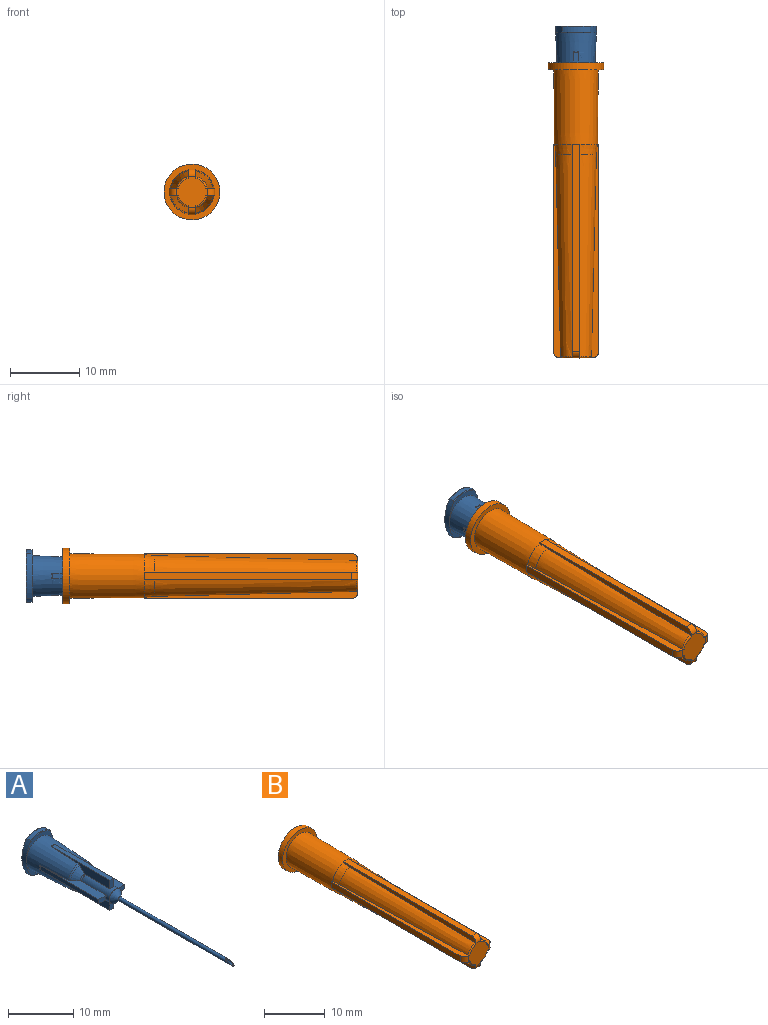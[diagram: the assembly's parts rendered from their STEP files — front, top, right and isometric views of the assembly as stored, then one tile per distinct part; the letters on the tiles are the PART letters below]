
ASSEMBLY  parts=2 mates=1
PART A: 60 faces, bbox 6x43x8.4 mm
  f0: cone r=2.51mm half-angle=44deg, axis (0,1,0), area 3.1mm2, adj f19,f22,f50,f54
  f1: cone r=2.97mm half-angle=2.9deg, axis (0,1,0), area 130.1mm2, adj f6,f7,f8,f9,f10,f11,f12,f13
  f2: cone r=2.51mm half-angle=44deg, axis (0,1,0), area 3.1mm2, adj f14,f17,f51,f55
  f3: cone r=2.51mm half-angle=44deg, axis (0,1,0), area 3.1mm2, adj f8,f12,f52,f56
  f4: cylinder r=1.28mm len=6.08mm, axis (0,1,0), area 31.5mm2, adj f8,f9,f12,f14,f17,f19,f22,f24
  f5: cone r=2.51mm half-angle=44deg, axis (0,1,0), area 3.1mm2, adj f9,f24,f49,f53
  f6: plane 0.2x0.02mm, normal (0,1,0), area 0mm2, adj f1,f7,f8
  f7: plane 12.75x0.8mm, normal (0,0,1), area 10.2mm2, adj f1,f6,f8,f9,f10,f29
  f8: plane 12.82x1.67mm, normal (-1,0,0), area 11mm2, adj f1,f3,f4,f6,f7,f29,f52,f56
  f9: plane 12.82x1.67mm, normal (1,0,0), area 11mm2, adj f1,f4,f5,f7,f10,f29,f49,f53
  f10: plane 0.2x0.02mm, normal (0,1,0), area 0mm2, adj f1,f7,f9
  f11: plane 0.2x0.02mm, normal (0,1,0), area 0mm2, adj f1,f13,f14
  f12: plane 12.82x1.67mm, normal (0,0,1), area 11mm2, adj f1,f3,f4,f13,f15,f28,f52,f56
  f13: plane 12.75x0.8mm, normal (-1,0,0), area 10.2mm2, adj f1,f11,f12,f14,f15,f28
  f14: plane 12.82x1.67mm, normal (0,0,-1), area 11mm2, adj f1,f2,f4,f11,f13,f28,f51,f55
  f15: plane 0.2x0.02mm, normal (0,1,0), area 0mm2, adj f1,f12,f13
  f16: plane 0.2x0.02mm, normal (0,1,0), area 0mm2, adj f1,f17,f18
  f17: plane 12.82x1.67mm, normal (-1,0,0), area 11mm2, adj f1,f2,f4,f16,f18,f27,f51,f55
  f18: plane 12.75x0.8mm, normal (0,0,-1), area 10.2mm2, adj f1,f16,f17,f19,f20,f27
  f19: plane 12.82x1.67mm, normal (1,0,0), area 11mm2, adj f0,f1,f4,f18,f20,f27,f50,f54
  f20: plane 0.2x0.02mm, normal (0,1,0), area 0mm2, adj f1,f18,f19
  f21: plane 0.2x0.02mm, normal (0,1,0), area 0mm2, adj f1,f23,f24
  f22: plane 12.82x1.67mm, normal (0,0,-1), area 11mm2, adj f0,f1,f4,f23,f25,f26,f50,f54
  f23: plane 12.75x0.8mm, normal (1,0,0), area 10.2mm2, adj f1,f21,f22,f24,f25,f26
  f24: plane 12.82x1.67mm, normal (0,0,1), area 11mm2, adj f1,f4,f5,f21,f23,f26,f49,f53
  f25: plane 0.2x0.02mm, normal (0,1,0), area 0mm2, adj f1,f22,f23
  f26: plane 1.6x0.8mm, normal (0,-1,0), area 1.2mm2, adj f4,f22,f23,f24
  f27: plane 1.6x0.8mm, normal (0,-1,0), area 1.2mm2, adj f4,f17,f18,f19
  f28: plane 1.6x0.8mm, normal (0,-1,0), area 1.2mm2, adj f4,f12,f13,f14
  f29: plane 1.6x0.8mm, normal (0,-1,0), area 1.2mm2, adj f4,f7,f8,f9
  f30: cone r=1.28mm half-angle=44.9deg, axis (0,1,0), area 6.8mm2, adj f4,f34
  f31: cone r=2.57mm half-angle=2.9deg, axis (0,1,0), area 106.9mm2, adj f44,f57
  f32: cylinder r=0.88mm len=4.07mm, axis (0,1,0), area 22.5mm2, adj f58,f59
  f33: cone r=1mm half-angle=44.9deg, axis (0,1,0), area 1.3mm2, adj f35,f59
  f34: cylinder r=0.33mm len=24.7mm, axis (0,1,0), area 48.7mm2, adj f30,f36
  f35: cylinder r=0.25mm len=25mm, axis (0,-1,0), area 38.2mm2, adj f33,f36
  f36: plane 1.73x0.66mm, normal (0,-0.35,0.94), area 0.4mm2, adj f34,f35
  f37: plane 7.49x5.95mm, normal (0,1,0), area 16.5mm2, adj f39,f41,f44,f45,f46
  f38: cylinder r=3.85mm len=4.04mm, axis (0,-1,0), area 3.3mm2, adj f39,f41,f46,f48
  f39: cylinder r=6.09mm len=6.55mm, axis (0,-1,0), area 6.7mm2, adj f37,f38,f40,f42,f43,f45,f46,f47
  f40: cylinder r=3.85mm len=4.04mm, axis (0,-1,0), area 3.3mm2, adj f39,f41,f45,f47
  f41: cylinder r=6.09mm len=6.55mm, axis (0,-1,0), area 6.7mm2, adj f37,f38,f40,f42,f43,f45,f46,f47
  f42: plane 5.95x3.75mm, normal (0,-1,0), area 4.8mm2, adj f1,f39,f41,f48
  f43: plane 5.95x3.75mm, normal (0,-1,0), area 4.8mm2, adj f1,f39,f41,f47
  f44: cylinder r=2.56mm len=5.13mm, axis (0,1,0), area 15.6mm2, adj f31,f37
  f45: torus R=3.75mm, axis (0,1,0), area 0.7mm2, adj f37,f39,f40,f41
  f46: torus R=3.75mm, axis (0,1,0), area 0.7mm2, adj f37,f38,f39,f41
  f47: torus R=3.75mm, axis (0,1,0), area 0.7mm2, adj f39,f40,f41,f43
  f48: torus R=3.75mm, axis (0,1,0), area 0.7mm2, adj f38,f39,f41,f42
  f49: torus R=2.03mm, axis (0,1,0), area 1.1mm2, adj f1,f5,f9,f24
  f50: torus R=2.03mm, axis (0,1,0), area 1.1mm2, adj f0,f1,f19,f22
  f51: torus R=2.03mm, axis (0,1,0), area 1.1mm2, adj f1,f2,f14,f17
  f52: torus R=2.03mm, axis (0,1,0), area 1.1mm2, adj f1,f3,f8,f12
  f53: torus R=1.58mm, axis (0,-1,0), area 0.3mm2, adj f4,f5,f9,f24
  f54: torus R=1.58mm, axis (0,-1,0), area 0.3mm2, adj f0,f4,f19,f22
  f55: torus R=1.58mm, axis (0,-1,0), area 0.3mm2, adj f2,f4,f14,f17
  f56: torus R=1.58mm, axis (0,-1,0), area 0.3mm2, adj f3,f4,f8,f12
  f57: revolved ~4.4x4.4mm, area 24.9mm2, adj f31,f58
  f58: torus R=5.88mm, axis (0,1,0), area 19.5mm2, adj f32,f57
  f59: revolved ~1.76x1.76mm, area 3.8mm2, adj f32,f33
PART B: 58 faces, bbox 33.3x63.9x33.3 mm
  f0: cylinder r=4.05mm len=8.1mm, axis (0,-1,0), area 26.7mm2, adj f1,f2
  f1: plane 8.1x8.1mm, normal (0,1,0), area 29.9mm2, adj f0,f37
  f2: plane 8.1x8.1mm, normal (0,-1,0), area 18.9mm2, adj f0,f36
  f3: cylinder r=1mm len=1.15mm, axis (0,0,-1), area 1.8mm2, adj f11,f13,f14,f15
  f4: torus R=2.1mm, axis (0,-1,0), area 0.7mm2, adj f11,f15,f16,f17
  f5: cylinder r=1mm len=1.15mm, axis (1,0,0), area 1.8mm2, adj f11,f17,f18,f19
  f6: torus R=2.1mm, axis (0,-1,0), area 0.7mm2, adj f11,f19,f20,f21
  f7: cylinder r=1mm len=1.15mm, axis (0,0,1), area 1.8mm2, adj f11,f21,f22,f24
  f8: torus R=2.1mm, axis (0,-1,0), area 0.7mm2, adj f11,f23,f24,f25
  f9: torus R=2.1mm, axis (0,-1,0), area 0.7mm2, adj f11,f12,f13,f27
  f10: cylinder r=1mm len=1.15mm, axis (-1,0,0), area 1.8mm2, adj f11,f25,f26,f27
  f11: plane 4.6x4.6mm, normal (0,-1,0), area 14.9mm2, adj f3,f4,f5,f6,f7,f8,f9,f10
  f12: cone r=3mm half-angle=1.4deg, axis (0,1,0), area 87.7mm2, adj f9,f13,f27,f28
  f13: plane 31.02x1.3mm, normal (0,0,1), area 21.3mm2, adj f3,f9,f11,f12,f14,f28,f29
  f14: plane 30x1.15mm, normal (-1,0,0), area 34.5mm2, adj f3,f13,f15,f29
  f15: plane 31.02x1.3mm, normal (0,0,-1), area 21.3mm2, adj f3,f4,f11,f14,f16,f29,f30
  f16: cone r=3mm half-angle=1.4deg, axis (0,1,0), area 87.7mm2, adj f4,f15,f17,f30
  f17: plane 31.02x1.3mm, normal (-1,0,0), area 21.3mm2, adj f4,f5,f11,f16,f18,f30,f31
  f18: plane 30x1.15mm, normal (0,0,-1), area 34.5mm2, adj f5,f17,f19,f31
  f19: plane 31.02x1.3mm, normal (1,0,0), area 21.3mm2, adj f5,f6,f11,f18,f20,f31,f32
  f20: cone r=3mm half-angle=1.4deg, axis (0,1,0), area 87.7mm2, adj f6,f19,f21,f32
  f21: plane 31.02x1.3mm, normal (0,0,-1), area 21.3mm2, adj f6,f7,f11,f20,f22,f32,f33
  f22: plane 30x1.15mm, normal (1,0,0), area 34.5mm2, adj f7,f21,f24,f33
  f23: cone r=3mm half-angle=1.4deg, axis (0,1,0), area 87.7mm2, adj f8,f24,f25,f34
  f24: plane 31.02x1.3mm, normal (0,0,1), area 21.3mm2, adj f7,f8,f11,f22,f23,f33,f34
  f25: plane 31.02x1.3mm, normal (1,0,0), area 21.3mm2, adj f8,f10,f11,f23,f26,f34,f35
  f26: plane 30x1.15mm, normal (0,0,1), area 34.5mm2, adj f10,f25,f27,f35
  f27: plane 31.02x1.3mm, normal (-1,0,0), area 21.3mm2, adj f9,f10,f11,f12,f26,f28,f35
  f28: cone r=3.12mm half-angle=4.8deg, axis (0,1,0), area 5.5mm2, adj f12,f13,f27,f36
  f29: plane 1.15x0.23mm, normal (0,1,0), area 0.2mm2, adj f13,f14,f15,f36
  f30: cone r=3.12mm half-angle=4.8deg, axis (0,1,0), area 5.5mm2, adj f15,f16,f17,f36
  f31: plane 1.15x0.23mm, normal (0,1,0), area 0.2mm2, adj f17,f18,f19,f36
  f32: cone r=3.12mm half-angle=4.8deg, axis (0,1,0), area 5.5mm2, adj f19,f20,f21,f36
  f33: plane 1.15x0.23mm, normal (0,1,0), area 0.2mm2, adj f21,f22,f24,f36
  f34: cone r=3.12mm half-angle=4.8deg, axis (0,1,0), area 5.5mm2, adj f23,f24,f25,f36
  f35: plane 1.15x0.23mm, normal (0,1,0), area 0.2mm2, adj f25,f26,f27,f36
  f36: cone r=3.23mm half-angle=0.5deg, axis (0,1,0), area 214.5mm2, adj f2,f28,f29,f30,f31,f32,f33,f34
  f37: cylinder r=2.62mm len=5.25mm, axis (0,1,0), area 17.3mm2, adj f1,f40
  f38: cone r=2.53mm half-angle=4.8deg, axis (0,1,0), area 16.4mm2, adj f39,f40,f42,f44,f46,f47,f48,f49
  f39: cone r=2.4mm half-angle=1.4deg, axis (0,1,0), area 354.4mm2, adj f38,f41,f42,f43,f44,f45,f46,f47
  f40: cone r=2.63mm half-angle=0.5deg, axis (0,1,0), area 173.5mm2, adj f37,f38
  f41: plane 3.43x3.43mm, normal (0,1,0), area 9.2mm2, adj f39
  f42: plane 5.73x0.25mm, normal (1,0,0), area 0.1mm2, adj f38,f39,f43,f57
  f43: cylinder r=2.3mm len=1.23mm, axis (0,-1,0), area 1.4mm2, adj f39,f42,f44,f57
  f44: plane 5.73x0.25mm, normal (-1,0,0), area 0.1mm2, adj f38,f39,f43,f57
  f45: cylinder r=2.3mm len=1.23mm, axis (0,-1,0), area 1.4mm2, adj f39,f46,f47,f56
  f46: plane 5.73x0.25mm, normal (0,0,-1), area 0.1mm2, adj f38,f39,f45,f56
  f47: plane 5.73x0.25mm, normal (0,0,1), area 0.1mm2, adj f38,f39,f45,f56
  f48: plane 5.73x0.25mm, normal (-1,0,0), area 0.1mm2, adj f38,f39,f50,f55
  f49: plane 5.73x0.25mm, normal (1,0,0), area 0.1mm2, adj f38,f39,f50,f55
  f50: cylinder r=2.3mm len=1.23mm, axis (0,-1,0), area 1.4mm2, adj f39,f48,f49,f55
  f51: plane 5.73x0.25mm, normal (0,0,-1), area 0.1mm2, adj f38,f39,f53,f54
  f52: plane 5.73x0.25mm, normal (0,0,1), area 0.1mm2, adj f38,f39,f53,f54
  f53: cylinder r=2.3mm len=1.23mm, axis (0,-1,0), area 1.4mm2, adj f39,f51,f52,f54
  f54: torus R=47.3mm, axis (0,1,0), area 5.1mm2, adj f38,f51,f52,f53
  f55: torus R=47.3mm, axis (0,1,0), area 5.1mm2, adj f38,f48,f49,f50
  f56: torus R=47.3mm, axis (0,1,0), area 5.1mm2, adj f38,f45,f46,f47
  f57: torus R=47.3mm, axis (0,1,0), area 5.1mm2, adj f38,f42,f43,f44
PLACE A t=(-9.72,-2.63,-2.42)mm
PLACE B t=(-9.72,-8.01,-2.42)mm
MATE slider A.f0 <-> B.f0  axis (0,1,0) through (-9.72,-6.94,-2.42)mm
